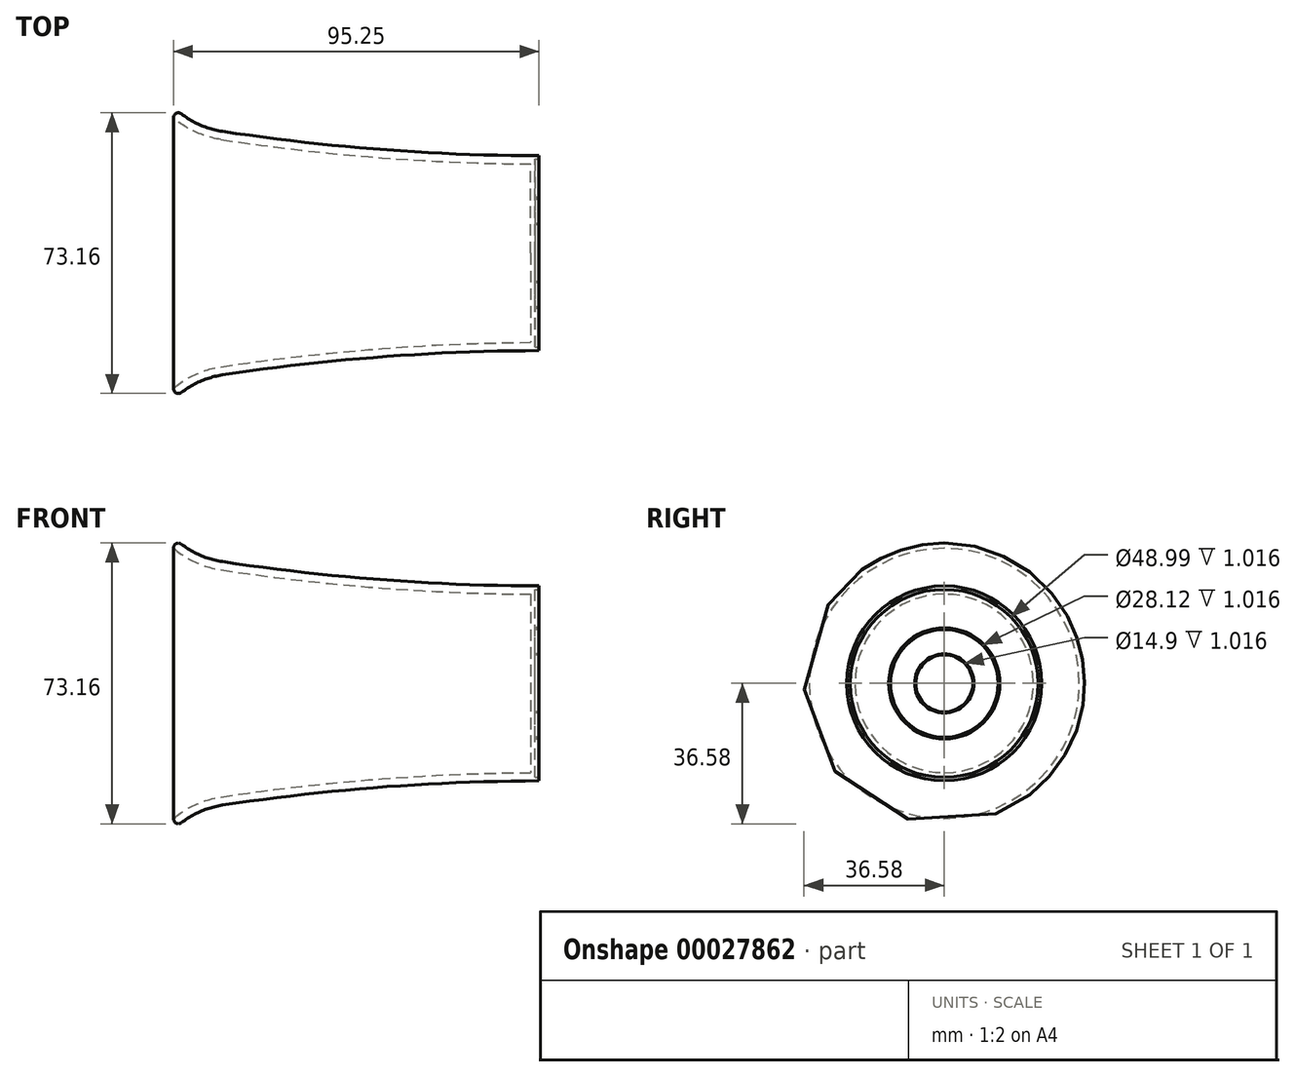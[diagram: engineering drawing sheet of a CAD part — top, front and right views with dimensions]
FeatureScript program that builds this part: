
annotation { "Feature Type Name" : "Feature", "Feature Type Description" : "" }
export const myFeature = defineFeature(function(context is Context, id is Id, definition is map)
    precondition{}
    {
        {
            var Q0;
            Q0=qCreatedBy(makeId("Front.planeOp"),FACE);
            var sketch = newSketch(context, id + "F0", { "sketchPlane" : qUnion([Q0])});
            skLineSegment(sketch, "E0", {"start": v(0, 0) * mm, "end": v(95.25, 0) * mm});
            skLineSegment(sketch, "E1", {"start": v(95.25, 0) * mm, "end": v(95.25, -25.4) * mm});
            skLineSegment(sketch, "E2", {"start": v(0, 0) * mm, "end": v(0, -38.1) * mm});
            skLineSegment(sketch, "E3", {"start": v(0, 0) * mm, "end": v(12.7, 0) * mm});
            skArc(sketch, "E4", {"start": v(12.7, -31.75) * mm, "mid": v(5.85, -33.92) * mm, "end": v(0, -38.1) * mm});
            skArc(sketch, "E5", {"start": v(95.25, -25.4) * mm, "mid": v(53.86, -27.06) * mm, "end": v(12.7, -31.75) * mm});
            skSolve(sketch);
        }
        {
            var Q0;
            Q0=makeQuery(id+"F0.imprint","IMPRINT",FACE,{"disambiguationData":[TD([[makeQuery(id+"F0.imprint","IMPRINT",EDGE,{"derivedFrom":sQuery(id+"F0.wireOp",EDGE,"E0")}),-1.0]])]});
            var Q1;
            Q1=sQuery(id+"F0.wireOp",EDGE,"E0");
            revolve(context, id + "F1", {"entities" : qUnion([Q0]), "axis" : qUnion([Q1]), "revolveType" : RevolveType.FULL});
        }
        {
            var Q0;
            Q0=makeQuery(id+"F1.opRevolve","SWEPT_FACE",FACE,{"disambiguationData":[OSD([sQuery(id+"F0.wireOp",EDGE,"E2")])]});
            shell(context, id + "F2", {"entities" : qUnion([Q0]), "thickness" : 2.16 * mm});
        }
        {
            var Q0;
            Q0=makeQuery(id+"F1.opRevolve","SWEPT_FACE",FACE,{"disambiguationData":[OSD([sQuery(id+"F0.wireOp",EDGE,"E1")])]});
            var sketch = newSketch(context, id + "F3", { "sketchPlane" : qUnion([Q0])});
            skCircle(sketch, "E6", {"center": v(0, 0) * mm, "radius": 24.5 * mm});
            skSolve(sketch);
        }
        {
            var Q0;
            Q0=makeQuery(id+"F3.imprint","IMPRINT",FACE,{"disambiguationData":[TD([[makeQuery(id+"F3.imprint","IMPRINT",EDGE,{"derivedFrom":sQuery(id+"F3.wireOp",EDGE,"E6")}),1.0]])]});
            extrude(context, id + "F4", {"entities" : qUnion([Q0]), "operationType" : NewBodyOperationType.REMOVE, "oppositeDirection" : true, "depth" : 1.02 * mm});
        }
        {
            var Q0;
            Q0=makeQuery(id+"F1.opRevolve","SWEPT_EDGE",EDGE,{"disambiguationData":[OSD([sQuery(id+"F0.wireOp",EDGE,"E2"),sQuery(id+"F0.wireOp",EDGE,"E4")])]});
            fillet(context, id + "F5", {"entities" : qUnion([Q0]), "radius" : 1.27 * mm, "tangentPropagation" : true, "allowEdgeOverflow" : false});
        }
        {
            var Q0;
            Q0=makeQuery(id+"F4.boolean.opBoolean","COPY",FACE,{"derivedFrom":makeQuery(id+"F4.opExtrude","CAP_FACE",FACE,{"disambiguationData":[OSD([sQuery(id+"F3.wireOp",EDGE,"E6")])],"isStart":false})});
            var sketch = newSketch(context, id + "F6", { "sketchPlane" : qUnion([Q0])});
            skCircle(sketch, "E7.0", {"center": v(0, 0) * mm, "radius": 14.48 * mm});
            skCircle(sketch, "E8.0", {"center": v(0, 0) * mm, "radius": 14.06 * mm});
            skSolve(sketch);
        }
        {
            var Q0;
            Q0=makeQuery(id+"F6.imprint","IMPRINT",FACE,{"disambiguationData":[TD([[makeQuery(id+"F6.imprint","IMPRINT",EDGE,{"derivedFrom":sQuery(id+"F6.wireOp",EDGE,"E7.0")}),1.0]])]});
            extrude(context, id + "F7", {"entities" : qUnion([Q0]), "operationType" : NewBodyOperationType.ADD, "depth" : 1.02 * mm});
        }
        {
            var Q0;
            Q0=makeQuery(id+"F7.boolean.opBoolean","SPLIT",FACE,{"disambiguationData":[TD([makeQuery(id+"F7.opExtrude","SWEPT_FACE",FACE,{"disambiguationData":[OSD([sQuery(id+"F6.wireOp",EDGE,"E8.0")])]})])],"derivedFrom":makeQuery(id+"F4.boolean.opBoolean","COPY",FACE,{"derivedFrom":makeQuery(id+"F4.opExtrude","CAP_FACE",FACE,{"disambiguationData":[OSD([sQuery(id+"F3.wireOp",EDGE,"E6")])],"isStart":false})})});
            var sketch = newSketch(context, id + "F8", { "sketchPlane" : qUnion([Q0])});
            skCircle(sketch, "E9.0", {"center": v(0, 0) * mm, "radius": 7.7 * mm});
            skCircle(sketch, "E10.0", {"center": v(0, 0) * mm, "radius": 7.45 * mm});
            skSolve(sketch);
        }
        {
            var Q0;
            Q0=makeQuery(id+"F8.imprint","IMPRINT",FACE,{"disambiguationData":[TD([[makeQuery(id+"F8.imprint","IMPRINT",EDGE,{"derivedFrom":sQuery(id+"F8.wireOp",EDGE,"E9.0")}),1.0]])]});
            extrude(context, id + "F9", {"entities" : qUnion([Q0]), "operationType" : NewBodyOperationType.ADD, "depth" : 1.02 * mm});
        }
    });
